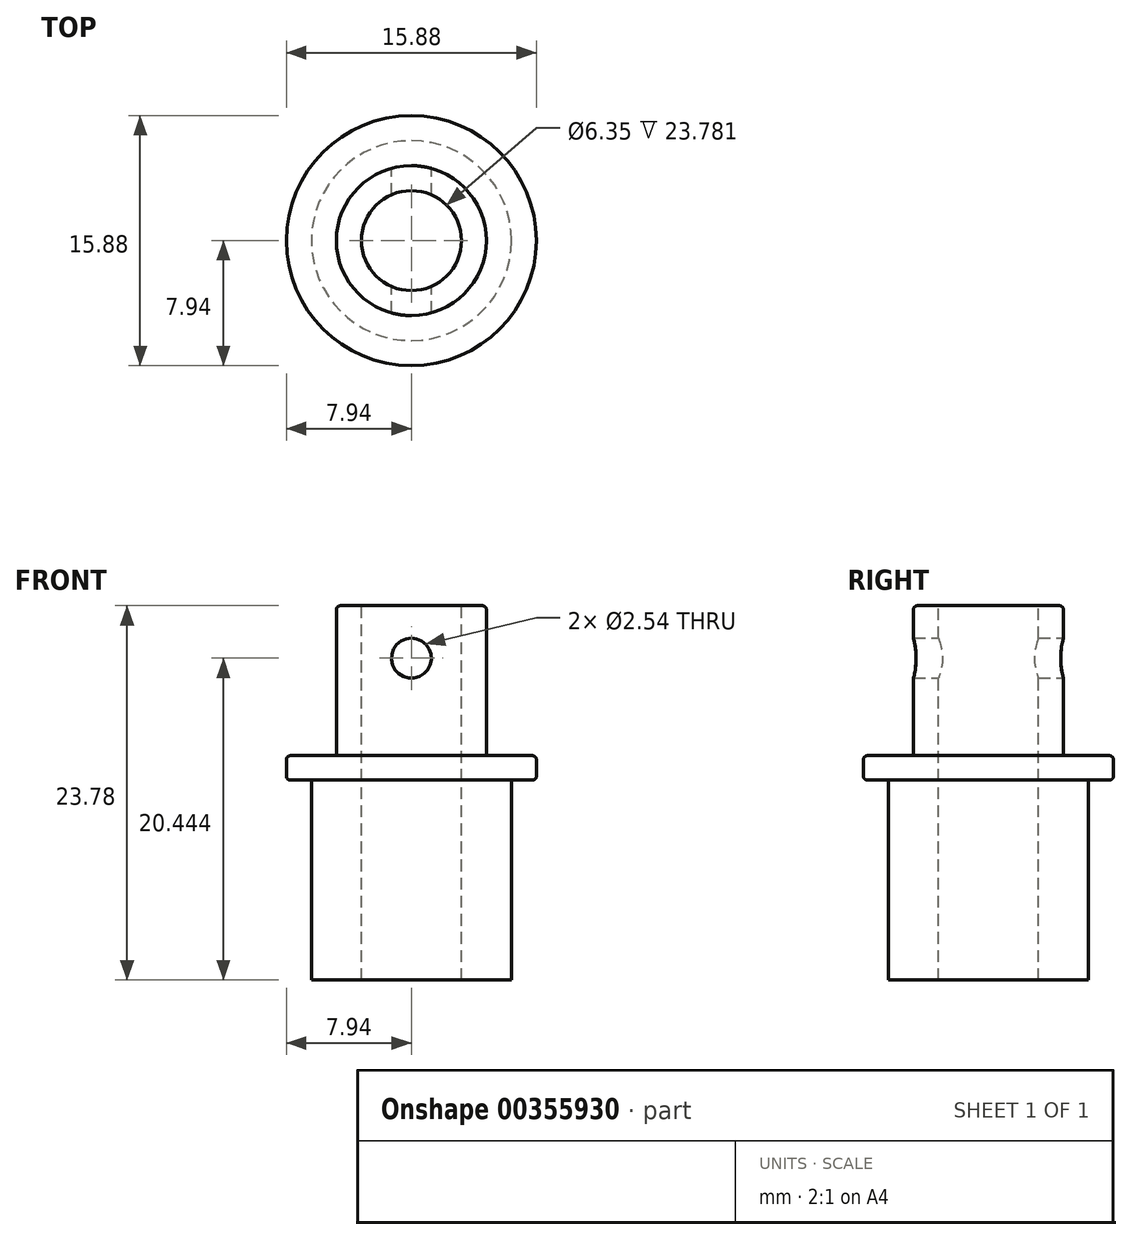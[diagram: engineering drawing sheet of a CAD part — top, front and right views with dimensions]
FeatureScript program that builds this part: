
annotation { "Feature Type Name" : "Feature", "Feature Type Description" : "" }
export const myFeature = defineFeature(function(context is Context, id is Id, definition is map)
    precondition{}
    {
        {
            var Q0;
            Q0=qCreatedBy(makeId("Top.planeOp"),FACE);
            var sketch = newSketch(context, id + "F0", { "sketchPlane" : qUnion([Q0])});
            skCircle(sketch, "E0", {"center": v(0, 0) * mm, "radius": 6.35 * mm});
            skSolve(sketch);
        }
        {
            var Q0;
            Q0=qSketchRegion(id+"F0",true);
            extrude(context, id + "F1", {"entities" : qUnion([Q0]), "oppositeDirection" : true, "depth" : 12.7 * mm});
        }
        {
            var Q0;
            Q0=makeQuery(id+"F1.opExtrude","CAP_FACE",FACE,{"disambiguationData":[OSD([sQuery(id+"F0.wireOp",EDGE,"E0")])],"isStart":true});
            var sketch = newSketch(context, id + "F2", { "sketchPlane" : qUnion([Q0])});
            skCircle(sketch, "E1", {"center": v(0, 0) * mm, "radius": 7.94 * mm});
            skSolve(sketch);
        }
        {
            var Q0;
            Q0=qSketchRegion(id+"F2",true);
            extrude(context, id + "F3", {"entities" : qUnion([Q0]), "operationType" : NewBodyOperationType.ADD, "depth" : 1.56 * mm});
        }
        {
            var Q0;
            Q0=makeQuery(id+"F3.opExtrude","CAP_FACE",FACE,{"disambiguationData":[OSD([sQuery(id+"F2.wireOp",EDGE,"E1")])],"isStart":false});
            var sketch = newSketch(context, id + "F4", { "sketchPlane" : qUnion([Q0])});
            skCircle(sketch, "E2", {"center": v(0, 0) * mm, "radius": 4.76 * mm});
            skSolve(sketch);
        }
        {
            var Q0;
            Q0=makeQuery(id+"F4.imprint","IMPRINT",FACE,{"disambiguationData":[TD([[makeQuery(id+"F4.imprint","IMPRINT",EDGE,{"derivedFrom":sQuery(id+"F4.wireOp",EDGE,"E2")}),1.0]])]});
            extrude(context, id + "F5", {"entities" : qUnion([Q0]), "operationType" : NewBodyOperationType.ADD, "depth" : 9.52 * mm});
        }
        {
            var Q0;
            Q0=makeQuery(id+"F3.opExtrude","CAP_EDGE",EDGE,{"disambiguationData":[OSD([sQuery(id+"F2.wireOp",EDGE,"E1")])],"isStart":false});
            var Q1;
            Q1=makeQuery(id+"F3.opExtrude","CAP_EDGE",EDGE,{"disambiguationData":[OSD([sQuery(id+"F2.wireOp",EDGE,"E1")])],"isStart":true});
            var Q2;
            Q2=makeQuery(id+"F5.opExtrude","CAP_EDGE",EDGE,{"disambiguationData":[OSD([sQuery(id+"F4.wireOp",EDGE,"E2")])],"isStart":false});
            fillet(context, id + "F6", {"entities" : qUnion([Q0, Q1, Q2]), "radius" : 0.25 * mm, "tangentPropagation" : true, "allowEdgeOverflow" : false});
        }
        {
            var Q0;
            Q0=qCreatedBy(makeId("Front.planeOp"),FACE);
            var sketch = newSketch(context, id + "F7", { "sketchPlane" : qUnion([Q0])});
            skCircle(sketch, "E3", {"center": v(0, 7.74) * mm, "radius": 1.27 * mm});
            skSolve(sketch);
        }
        {
            var Q0;
            Q0=qSketchRegion(id+"F7",true);
            extrude(context, id + "F8", {"entities" : qUnion([Q0]), "operationType" : NewBodyOperationType.REMOVE, "endBound" : BoundingType.SYMMETRIC, "depth" : 25.4 * mm});
        }
        {
            var Q0;
            Q0=makeQuery(id+"F5.opExtrude","CAP_FACE",FACE,{"disambiguationData":[OSD([sQuery(id+"F4.wireOp",EDGE,"E2")])],"isStart":false});
            var sketch = newSketch(context, id + "F9", { "sketchPlane" : qUnion([Q0])});
            skCircle(sketch, "E4", {"center": v(0, 0) * mm, "radius": 3.18 * mm});
            skSolve(sketch);
        }
        {
            var Q0;
            Q0=makeQuery(id+"F9.imprint","IMPRINT",FACE,{"disambiguationData":[TD([[makeQuery(id+"F9.imprint","IMPRINT",EDGE,{"derivedFrom":sQuery(id+"F9.wireOp",EDGE,"E4")}),1.0]])]});
            extrude(context, id + "F10", {"entities" : qUnion([Q0]), "operationType" : NewBodyOperationType.REMOVE, "endBound" : BoundingType.THROUGH_ALL, "oppositeDirection" : true, "depth" : 25.4 * mm});
        }
    });
